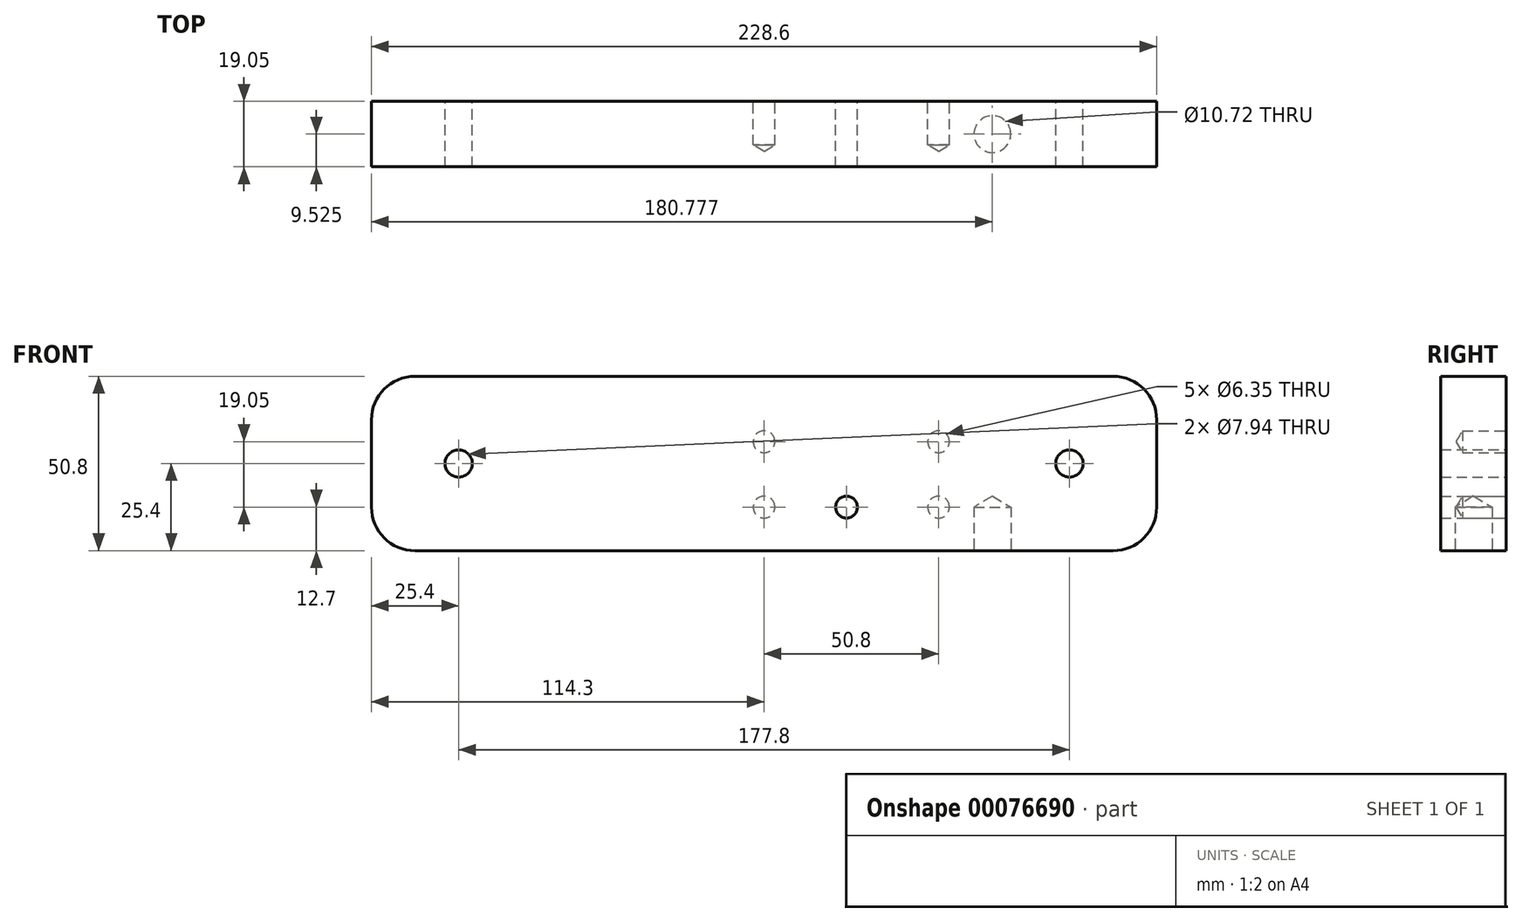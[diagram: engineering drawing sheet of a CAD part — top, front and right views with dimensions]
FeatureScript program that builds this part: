
annotation { "Feature Type Name" : "Feature", "Feature Type Description" : "" }
export const myFeature = defineFeature(function(context is Context, id is Id, definition is map)
    precondition{}
    {
        {
            var Q0;
            Q0=qCreatedBy(makeId("Front.planeOp"),FACE);
            var sketch = newSketch(context, id + "F0", { "sketchPlane" : qUnion([Q0])});
            skLineSegment(sketch, "E0.bottom", {"start": v(0, 0) * mm, "end": v(-228.6, 0) * mm});
            skLineSegment(sketch, "E0.top", {"start": v(0, 50.8) * mm, "end": v(-228.6, 50.8) * mm});
            skLineSegment(sketch, "E0.left", {"start": v(0, 0) * mm, "end": v(0, 50.8) * mm});
            skLineSegment(sketch, "E0.right", {"start": v(-228.6, 0) * mm, "end": v(-228.6, 50.8) * mm});
            skLineSegment(sketch, "E1.0", {"start": v(-203.2, 0) * mm, "end": v(-203.2, 50.8) * mm, "construction": true});
            skLineSegment(sketch, "E2.0", {"start": v(-25.4, 0) * mm, "end": v(-25.4, 50.8) * mm, "construction": true});
            skLineSegment(sketch, "E3.0", {"start": v(-63.5, 0) * mm, "end": v(-63.5, 50.8) * mm, "construction": true});
            skLineSegment(sketch, "E4.0", {"start": v(-114.3, 0) * mm, "end": v(-114.3, 50.8) * mm, "construction": true});
            skLineSegment(sketch, "E5.0", {"start": v(-90.3, 0) * mm, "end": v(-90.3, 50.8) * mm, "construction": true});
            skLineSegment(sketch, "E6.0", {"start": v(0, 12.7) * mm, "end": v(-228.6, 12.7) * mm, "construction": true});
            skLineSegment(sketch, "E7.0", {"start": v(0, 31.75) * mm, "end": v(-228.6, 31.75) * mm, "construction": true});
            skLineSegment(sketch, "E8.0", {"start": v(0, 25.4) * mm, "end": v(-228.6, 25.4) * mm, "construction": true});
            skCircle(sketch, "E9", {"center": v(-25.4, 25.4) * mm, "radius": 3.97 * mm, "construction": true});
            skCircle(sketch, "E10", {"center": v(-63.5, 12.7) * mm, "radius": 3.18 * mm, "construction": true});
            skCircle(sketch, "E11", {"center": v(-63.5, 31.75) * mm, "radius": 3.18 * mm, "construction": true});
            skCircle(sketch, "E12", {"center": v(-90.3, 12.7) * mm, "radius": 3.18 * mm, "construction": true});
            skCircle(sketch, "E13", {"center": v(-114.3, 12.7) * mm, "radius": 3.18 * mm, "construction": true});
            skCircle(sketch, "E14", {"center": v(-114.3, 31.75) * mm, "radius": 3.18 * mm, "construction": true});
            skCircle(sketch, "E15", {"center": v(-203.2, 25.4) * mm, "radius": 3.97 * mm, "construction": true});
            skSolve(sketch);
        }
        {
            var Q0;
            Q0=makeQuery(id+"F0.imprint","IMPRINT",FACE,{"disambiguationData":[TD([[makeQuery(id+"F0.imprint","IMPRINT",EDGE,{"derivedFrom":sQuery(id+"F0.wireOp",EDGE,"E0.bottom")}),-1.0]])]});
            extrude(context, id + "F1", {"entities" : qUnion([Q0]), "depth" : 19.05 * mm});
        }
        {
            var Q0;
            Q0=sQuery(id+"F0.wireOp",VERTEX,"E15.center");
            var Q1;
            Q1=sQuery(id+"F0.wireOp",VERTEX,"E9.center");
            var Q2;
            Q2=makeQuery(id+"F1.opExtrude","SWEPT_BODY",BODY,{"disambiguationData":[OSD([sQuery(id+"F0.wireOp",EDGE,"E0.bottom"),sQuery(id+"F0.wireOp",EDGE,"E0.top"),sQuery(id+"F0.wireOp",EDGE,"E0.left"),sQuery(id+"F0.wireOp",EDGE,"E0.right")])]});
            hole(context, id + "F2", {"style" : HoleStyle.SIMPLE, "endStyle" : HoleEndStyle.THROUGH, "oppositeDirection" : true, "holeDiameter" : 7.94 * mm, "locations" : qUnion([Q0, Q1]), "scope" : qUnion([Q2]), "isTappedThrough" : true});
        }
        {
            var Q0;
            Q0=makeQuery(id+"F1.opExtrude","SWEPT_EDGE",EDGE,{"disambiguationData":[OSD([sQuery(id+"F0.wireOp",EDGE,"E0.bottom"),sQuery(id+"F0.wireOp",EDGE,"E0.left")])]});
            var Q1;
            Q1=makeQuery(id+"F1.opExtrude","SWEPT_EDGE",EDGE,{"disambiguationData":[OSD([sQuery(id+"F0.wireOp",EDGE,"E0.top"),sQuery(id+"F0.wireOp",EDGE,"E0.left")])]});
            fillet(context, id + "F3", {"entities" : qUnion([Q0, Q1]), "radius" : 12.7 * mm, "tangentPropagation" : true, "allowEdgeOverflow" : false});
        }
        {
            var Q0;
            Q0=sQuery(id+"F0.wireOp",VERTEX,"E14.center");
            var Q1;
            Q1=sQuery(id+"F0.wireOp",VERTEX,"E13.center");
            var Q2;
            Q2=sQuery(id+"F0.wireOp",VERTEX,"E10.center");
            var Q3;
            Q3=sQuery(id+"F0.wireOp",VERTEX,"E11.center");
            var Q4;
            Q4=makeQuery(id+"F1.opExtrude","SWEPT_BODY",BODY,{"disambiguationData":[OSD([sQuery(id+"F0.wireOp",EDGE,"E0.bottom"),sQuery(id+"F0.wireOp",EDGE,"E0.top"),sQuery(id+"F0.wireOp",EDGE,"E0.left"),sQuery(id+"F0.wireOp",EDGE,"E0.right")])]});
            hole(context, id + "F4", {"style" : HoleStyle.SIMPLE, "endStyle" : HoleEndStyle.BLIND, "oppositeDirection" : true, "holeDiameter" : 6.35 * mm, "holeDepth" : 12.7 * mm, "locations" : qUnion([Q0, Q1, Q2, Q3]), "scope" : qUnion([Q4])});
        }
        {
            var Q0;
            Q0=makeQuery(id+"F1.opExtrude","SWEPT_BODY",BODY,{"disambiguationData":[OSD([sQuery(id+"F0.wireOp",EDGE,"E0.bottom"),sQuery(id+"F0.wireOp",EDGE,"E0.top"),sQuery(id+"F0.wireOp",EDGE,"E0.left"),sQuery(id+"F0.wireOp",EDGE,"E0.right")])]});
            var Q1;
            Q1=makeQuery(id+"F1.opExtrude","CAP_FACE",FACE,{"disambiguationData":[OSD([sQuery(id+"F0.wireOp",EDGE,"E0.bottom"),sQuery(id+"F0.wireOp",EDGE,"E0.top"),sQuery(id+"F0.wireOp",EDGE,"E0.left"),sQuery(id+"F0.wireOp",EDGE,"E0.right")])],"isStart":false});
            mirror(context, id + "F5", {"entities" : qUnion([Q0]), "mirrorPlane" : qUnion([Q1])});
        }
        {
            var Q0;
            Q0=makeQuery(id+"F1.opExtrude","SWEPT_BODY",BODY,{"disambiguationData":[OSD([sQuery(id+"F0.wireOp",EDGE,"E0.bottom"),sQuery(id+"F0.wireOp",EDGE,"E0.top"),sQuery(id+"F0.wireOp",EDGE,"E0.left"),sQuery(id+"F0.wireOp",EDGE,"E0.right")])]});
            deleteBodies(context, id + "F6", {"entities" : qUnion([Q0])});
        }
        {
            var Q0;
            Q0=makeQuery(id+"F5.opPattern","COPY",BODY,{"derivedFrom":makeQuery(id+"F1.opExtrude","SWEPT_BODY",BODY,{"disambiguationData":[OSD([sQuery(id+"F0.wireOp",EDGE,"E0.bottom"),sQuery(id+"F0.wireOp",EDGE,"E0.top"),sQuery(id+"F0.wireOp",EDGE,"E0.left"),sQuery(id+"F0.wireOp",EDGE,"E0.right")])]}),"instanceName":"1"});
            var Q1;
            Q1=makeQuery(id+"F5.opPattern","COPY",FACE,{"derivedFrom":makeQuery(id+"F1.opExtrude","CAP_FACE",FACE,{"disambiguationData":[OSD([sQuery(id+"F0.wireOp",EDGE,"E0.bottom"),sQuery(id+"F0.wireOp",EDGE,"E0.top"),sQuery(id+"F0.wireOp",EDGE,"E0.left"),sQuery(id+"F0.wireOp",EDGE,"E0.right")])],"isStart":false}),"instanceName":"1"});
            mirror(context, id + "F7", {"entities" : qUnion([Q0]), "mirrorPlane" : qUnion([Q1])});
        }
        {
            var Q0;
            Q0=makeQuery(id+"F5.opPattern","COPY",BODY,{"derivedFrom":makeQuery(id+"F1.opExtrude","SWEPT_BODY",BODY,{"disambiguationData":[OSD([sQuery(id+"F0.wireOp",EDGE,"E0.bottom"),sQuery(id+"F0.wireOp",EDGE,"E0.top"),sQuery(id+"F0.wireOp",EDGE,"E0.left"),sQuery(id+"F0.wireOp",EDGE,"E0.right")])]}),"instanceName":"1"});
            deleteBodies(context, id + "F8", {"entities" : qUnion([Q0])});
        }
        {
            var Q0;
            Q0=sQuery(id+"F0.wireOp",VERTEX,"E12.center");
            var Q1;
            Q1=makeQuery(id+"F7.opPattern","COPY",BODY,{"derivedFrom":makeQuery(id+"F5.opPattern","COPY",BODY,{"derivedFrom":makeQuery(id+"F1.opExtrude","SWEPT_BODY",BODY,{"disambiguationData":[OSD([sQuery(id+"F0.wireOp",EDGE,"E0.bottom"),sQuery(id+"F0.wireOp",EDGE,"E0.top"),sQuery(id+"F0.wireOp",EDGE,"E0.left"),sQuery(id+"F0.wireOp",EDGE,"E0.right")])]}),"instanceName":"1"}),"instanceName":"1"});
            hole(context, id + "F9", {"style" : HoleStyle.SIMPLE, "endStyle" : HoleEndStyle.THROUGH, "oppositeDirection" : true, "holeDiameter" : 6.35 * mm, "locations" : qUnion([Q0]), "scope" : qUnion([Q1]), "isTappedThrough" : true});
        }
        {
            var Q0;
            Q0=makeQuery(id+"F7.opPattern","COPY",EDGE,{"derivedFrom":makeQuery(id+"F5.opPattern","COPY",EDGE,{"derivedFrom":makeQuery(id+"F1.opExtrude","SWEPT_EDGE",EDGE,{"disambiguationData":[OSD([sQuery(id+"F0.wireOp",EDGE,"E0.top"),sQuery(id+"F0.wireOp",EDGE,"E0.right")])]}),"instanceName":"1"}),"instanceName":"1"});
            var Q1;
            Q1=makeQuery(id+"F7.opPattern","COPY",EDGE,{"derivedFrom":makeQuery(id+"F5.opPattern","COPY",EDGE,{"derivedFrom":makeQuery(id+"F1.opExtrude","SWEPT_EDGE",EDGE,{"disambiguationData":[OSD([sQuery(id+"F0.wireOp",EDGE,"E0.bottom"),sQuery(id+"F0.wireOp",EDGE,"E0.right")])]}),"instanceName":"1"}),"instanceName":"1"});
            fillet(context, id + "F10", {"entities" : qUnion([Q0, Q1]), "radius" : 12.7 * mm, "tangentPropagation" : true, "allowEdgeOverflow" : false});
        }
        {
            var Q0;
            Q0=makeQuery(id+"F7.opPattern","COPY",FACE,{"derivedFrom":makeQuery(id+"F5.opPattern","COPY",FACE,{"derivedFrom":makeQuery(id+"F1.opExtrude","SWEPT_FACE",FACE,{"disambiguationData":[OSD([sQuery(id+"F0.wireOp",EDGE,"E0.bottom")])]}),"instanceName":"1"}),"instanceName":"1"});
            var sketch = newSketch(context, id + "F11", { "sketchPlane" : qUnion([Q0])});
            skLineSegment(sketch, "E16", {"start": v(-228.8, 9.53) * mm, "end": v(-47.82, 9.53) * mm, "construction": true});
            skPoint(sketch, "E16.startSnap0", {"position": v(-215.9, 9.53) * mm});
            skCircle(sketch, "E17", {"center": v(-47.82, 9.53) * mm, "radius": 5.36 * mm});
            skSolve(sketch);
        }
        {
            var Q0;
            Q0=sQuery(id+"F11.wireOp",VERTEX,"E17.center");
            var Q1;
            Q1=makeQuery(id+"F7.opPattern","COPY",BODY,{"derivedFrom":makeQuery(id+"F5.opPattern","COPY",BODY,{"derivedFrom":makeQuery(id+"F1.opExtrude","SWEPT_BODY",BODY,{"disambiguationData":[OSD([sQuery(id+"F0.wireOp",EDGE,"E0.bottom"),sQuery(id+"F0.wireOp",EDGE,"E0.top"),sQuery(id+"F0.wireOp",EDGE,"E0.left"),sQuery(id+"F0.wireOp",EDGE,"E0.right")])]}),"instanceName":"1"}),"instanceName":"1"});
            hole(context, id + "F12", {"style" : HoleStyle.SIMPLE, "endStyle" : HoleEndStyle.BLIND, "holeDiameter" : 10.72 * mm, "holeDepth" : 12.7 * mm, "locations" : qUnion([Q0]), "scope" : qUnion([Q1])});
        }
    });
